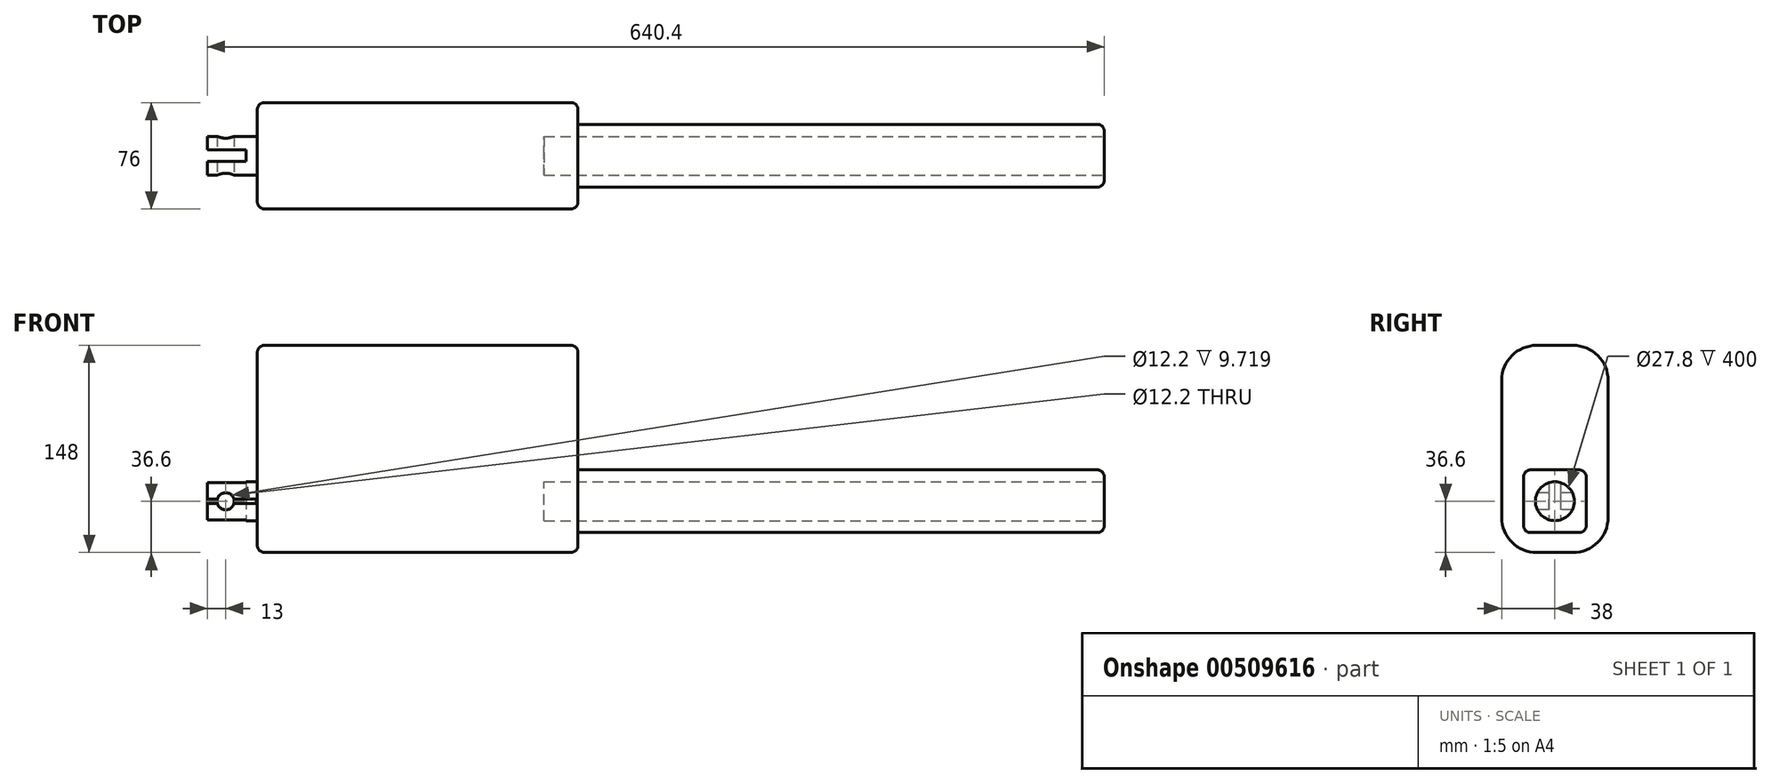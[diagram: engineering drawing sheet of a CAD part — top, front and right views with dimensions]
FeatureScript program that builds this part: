
annotation { "Feature Type Name" : "Feature", "Feature Type Description" : "" }
export const myFeature = defineFeature(function(context is Context, id is Id, definition is map)
    precondition{}
    {
        {
            var Q0;
            Q0=qCreatedBy(makeId("Front.planeOp"),FACE);
            var sketch = newSketch(context, id + "F0", { "sketchPlane" : qUnion([Q0])});
            skLineSegment(sketch, "E0.bottom", {"start": v(-114.5, 74) * mm, "end": v(114.5, 74) * mm});
            skLineSegment(sketch, "E0.top", {"start": v(-114.5, -74) * mm, "end": v(114.5, -74) * mm});
            skLineSegment(sketch, "E0.left", {"start": v(-114.5, 74) * mm, "end": v(-114.5, -74) * mm});
            skLineSegment(sketch, "E0.right", {"start": v(114.5, 74) * mm, "end": v(114.5, -74) * mm});
            skPoint(sketch, "E0.middle", {"position": v(0, 0) * mm});
            skSolve(sketch);
        }
        {
            var Q0;
            Q0=makeQuery(id+"F0.imprint","IMPRINT",FACE,{"disambiguationData":[TD([[makeQuery(id+"F0.imprint","IMPRINT",EDGE,{"derivedFrom":sQuery(id+"F0.wireOp",EDGE,"E0.bottom")}),-1.0]])]});
            extrude(context, id + "F1", {"entities" : qUnion([Q0]), "endBound" : BoundingType.SYMMETRIC, "depth" : 76 * mm});
        }
        {
            var Q0;
            Q0=makeQuery(id+"F1.opExtrude","SWEPT_FACE",FACE,{"disambiguationData":[OSD([sQuery(id+"F0.wireOp",EDGE,"E0.left")])]});
            var sketch = newSketch(context, id + "F2", { "sketchPlane" : qUnion([Q0])});
            skLineSegment(sketch, "E1", {"start": v(0, -74) * mm, "end": v(0, -37.4) * mm});
            skPoint(sketch, "E1.endSnap0", {"position": v(0, -74) * mm});
            skCircle(sketch, "E2", {"center": v(0, -37.4) * mm, "radius": 13.9 * mm});
            skSolve(sketch);
        }
        {
            var Q0;
            Q0=makeQuery(id+"F2.imprint","IMPRINT",FACE,{"disambiguationData":[TD([[makeQuery(id+"F2.imprint","IMPRINT",EDGE,{"derivedFrom":sQuery(id+"F2.wireOp",EDGE,"E2")}),1.0]])]});
            extrude(context, id + "F3", {"entities" : qUnion([Q0]), "operationType" : NewBodyOperationType.ADD, "depth" : 35.6 * mm});
        }
        {
            var Q0;
            Q0=makeQuery(id+"F3.opExtrude","CAP_FACE",FACE,{"disambiguationData":[OSD([sQuery(id+"F2.wireOp",EDGE,"E2")])],"isStart":false});
            var sketch = newSketch(context, id + "F4", { "sketchPlane" : qUnion([Q0])});
            skLineSegment(sketch, "E3.left", {"start": v(-13.82, -35.9) * mm, "end": v(-13.82, -38.9) * mm});
            skLineSegment(sketch, "E3.right", {"start": v(13.82, -35.9) * mm, "end": v(13.82, -38.9) * mm});
            skPoint(sketch, "E3.middle", {"position": v(0, -37.4) * mm});
            skSolve(sketch);
        }
        {
            var Q0;
            {var subQ0=sQuery(id+"F4.wireOp",EDGE,"E3.right");Q0=makeQuery(id+"F4.imprint","IMPRINT",FACE,{"disambiguationData":[TD([[makeQuery(id+"F4.imprint","IMPRINT",EDGE,{"derivedFrom":subQ0}),1.0]])]});}
            extrude(context, id + "F5", {"entities" : qUnion([Q0]), "operationType" : NewBodyOperationType.REMOVE, "oppositeDirection" : true, "depth" : 35 * mm});
        }
        {
            var Q0;
            Q0=makeQuery(id+"F5.boolean.opBoolean","COPY",FACE,{"derivedFrom":makeQuery(id+"F5.opExtrude","SWEPT_FACE",FACE,{"disambiguationData":[OSD([sQuery(id+"F4.wireOp",EDGE,"E3.right")])]})});
            var sketch = newSketch(context, id + "F6", { "sketchPlane" : qUnion([Q0])});
            skLineSegment(sketch, "E4", {"start": v(-150.1, -37.4) * mm, "end": v(-137.1, -37.4) * mm});
            skSolve(sketch);
        }
        {
            var Q0;
            Q0=sQuery(id+"F6.wireOp",VERTEX,"E4.end");
            var Q1;
            Q1=makeQuery(id+"F1.opExtrude","SWEPT_BODY",BODY,{"disambiguationData":[OSD([sQuery(id+"F0.wireOp",EDGE,"E0.bottom"),sQuery(id+"F0.wireOp",EDGE,"E0.top"),sQuery(id+"F0.wireOp",EDGE,"E0.left"),sQuery(id+"F0.wireOp",EDGE,"E0.right")])]});
            hole(context, id + "F7", {"style" : HoleStyle.SIMPLE, "endStyle" : HoleEndStyle.THROUGH, "holeDiameter" : 12.2 * mm, "isTappedThrough" : true, "tappedDepth" : 12 * mm, "tapClearance" : 3, "locations" : qUnion([Q0]), "scope" : qUnion([Q1])});
        }
        {
            var Q0;
            Q0=makeQuery(id+"F1.opExtrude","SWEPT_FACE",FACE,{"disambiguationData":[OSD([sQuery(id+"F0.wireOp",EDGE,"E0.right")])]});
            var sketch = newSketch(context, id + "F8", { "sketchPlane" : qUnion([Q0])});
            skLineSegment(sketch, "E5", {"start": v(0, -74) * mm, "end": v(0, -37.4) * mm});
            skLineSegment(sketch, "E6.bottom", {"start": v(-22.4, -15) * mm, "end": v(22.4, -15) * mm});
            skLineSegment(sketch, "E6.top", {"start": v(-22.4, -59.8) * mm, "end": v(22.4, -59.8) * mm});
            skLineSegment(sketch, "E6.left", {"start": v(-22.4, -15) * mm, "end": v(-22.4, -59.8) * mm});
            skLineSegment(sketch, "E6.right", {"start": v(22.4, -15) * mm, "end": v(22.4, -59.8) * mm});
            skPoint(sketch, "E6.middle", {"position": v(0, -37.4) * mm});
            skSolve(sketch);
        }
        {
            var Q0;
            Q0=makeQuery(id+"F8.imprint","IMPRINT",FACE,{"disambiguationData":[TD([[makeQuery(id+"F8.imprint","IMPRINT",EDGE,{"derivedFrom":sQuery(id+"F8.wireOp",EDGE,"E6.bottom")}),-1.0]])]});
            extrude(context, id + "F9", {"entities" : qUnion([Q0]), "operationType" : NewBodyOperationType.ADD, "depth" : 375.8 * mm});
        }
        {
            var Q0;
            Q0=makeQuery(id+"F9.opExtrude","CAP_FACE",FACE,{"disambiguationData":[OSD([sQuery(id+"F8.wireOp",EDGE,"E6.bottom"),sQuery(id+"F8.wireOp",EDGE,"E6.top"),sQuery(id+"F8.wireOp",EDGE,"E6.left"),sQuery(id+"F8.wireOp",EDGE,"E6.right")])],"isStart":false});
            var sketch = newSketch(context, id + "F10", { "sketchPlane" : qUnion([Q0])});
            skLineSegment(sketch, "E7", {"start": v(0, -15) * mm, "end": v(0, -37.4) * mm});
            skPoint(sketch, "E7.endSnap0", {"position": v(0, -15) * mm});
            skCircle(sketch, "E8", {"center": v(0, -37.4) * mm, "radius": 13.9 * mm});
            skSolve(sketch);
        }
        {
            var Q0;
            Q0=makeQuery(id+"F1.opExtrude","CAP_EDGE",EDGE,{"disambiguationData":[OSD([sQuery(id+"F0.wireOp",EDGE,"E0.bottom")])],"isStart":false});
            var Q1;
            Q1=makeQuery(id+"F1.opExtrude","CAP_EDGE",EDGE,{"disambiguationData":[OSD([sQuery(id+"F0.wireOp",EDGE,"E0.bottom")])],"isStart":true});
            var Q2;
            Q2=makeQuery(id+"F1.opExtrude","CAP_EDGE",EDGE,{"disambiguationData":[OSD([sQuery(id+"F0.wireOp",EDGE,"E0.top")])],"isStart":false});
            var Q3;
            Q3=makeQuery(id+"F1.opExtrude","CAP_EDGE",EDGE,{"disambiguationData":[OSD([sQuery(id+"F0.wireOp",EDGE,"E0.top")])],"isStart":true});
            fillet(context, id + "F11", {"entities" : qUnion([Q0, Q1, Q2, Q3]), "radius" : 25 * mm, "tangentPropagation" : true, "allowEdgeOverflow" : false});
        }
        {
            var Q0;
            Q0=makeQuery(id+"F9.opExtrude","SWEPT_EDGE",EDGE,{"disambiguationData":[OSD([sQuery(id+"F8.wireOp",EDGE,"E6.bottom"),sQuery(id+"F8.wireOp",EDGE,"E6.left")])]});
            var Q1;
            Q1=makeQuery(id+"F9.opExtrude","SWEPT_EDGE",EDGE,{"disambiguationData":[OSD([sQuery(id+"F8.wireOp",EDGE,"E6.bottom"),sQuery(id+"F8.wireOp",EDGE,"E6.right")])]});
            var Q2;
            Q2=makeQuery(id+"F9.opExtrude","SWEPT_EDGE",EDGE,{"disambiguationData":[OSD([sQuery(id+"F8.wireOp",EDGE,"E6.top"),sQuery(id+"F8.wireOp",EDGE,"E6.left")])]});
            var Q3;
            Q3=makeQuery(id+"F9.opExtrude","SWEPT_EDGE",EDGE,{"disambiguationData":[OSD([sQuery(id+"F8.wireOp",EDGE,"E6.top"),sQuery(id+"F8.wireOp",EDGE,"E6.right")])]});
            var Q4;
            Q4=makeQuery(id+"F1.opExtrude","CAP_EDGE",EDGE,{"disambiguationData":[OSD([sQuery(id+"F0.wireOp",EDGE,"E0.right")])],"isStart":true});
            var Q5;
            Q5=makeQuery(id+"F1.opExtrude","CAP_EDGE",EDGE,{"disambiguationData":[OSD([sQuery(id+"F0.wireOp",EDGE,"E0.left")])],"isStart":true});
            var Q6;
            Q6=makeQuery(id+"F9.opExtrude","CAP_EDGE",EDGE,{"disambiguationData":[OSD([sQuery(id+"F8.wireOp",EDGE,"E6.right")])],"isStart":false});
            var Q7;
            Q7=makeQuery(id+"F9.opExtrude","CAP_FACE",FACE,{"disambiguationData":[OSD([sQuery(id+"F8.wireOp",EDGE,"E6.bottom"),sQuery(id+"F8.wireOp",EDGE,"E6.top"),sQuery(id+"F8.wireOp",EDGE,"E6.left"),sQuery(id+"F8.wireOp",EDGE,"E6.right")])],"isStart":false});
            fillet(context, id + "F12", {"entities" : qUnion([Q0, Q1, Q2, Q3, Q4, Q5, Q6, Q7]), "radius" : 5 * mm, "tangentPropagation" : true, "allowEdgeOverflow" : false});
        }
        {
            var Q0;
            Q0=makeQuery(id+"F10.imprint","IMPRINT",FACE,{"disambiguationData":[TD([[makeQuery(id+"F10.imprint","IMPRINT",EDGE,{"derivedFrom":sQuery(id+"F10.wireOp",EDGE,"E8")}),1.0]])]});
            extrude(context, id + "F13", {"entities" : qUnion([Q0]), "operationType" : NewBodyOperationType.REMOVE, "oppositeDirection" : true, "depth" : 400 * mm});
        }
        {
            var Q0;
            Q0=makeQuery(id+"F3.opExtrude","CAP_FACE",FACE,{"disambiguationData":[OSD([sQuery(id+"F2.wireOp",EDGE,"E2")])],"isStart":false});
            var sketch = newSketch(context, id + "F14", { "sketchPlane" : qUnion([Q0])});
            skLineSegment(sketch, "E9.bottom", {"start": v(-4.1, 11.75) * mm, "end": v(4.1, 11.75) * mm});
            skLineSegment(sketch, "E9.top", {"start": v(-4.1, -86.55) * mm, "end": v(4.1, -86.55) * mm});
            skLineSegment(sketch, "E9.left", {"start": v(-4.1, 11.75) * mm, "end": v(-4.1, -86.55) * mm});
            skLineSegment(sketch, "E9.right", {"start": v(4.1, 11.75) * mm, "end": v(4.1, -86.55) * mm});
            skPoint(sketch, "E9.middle", {"position": v(0, -37.4) * mm});
            skSolve(sketch);
        }
        {
            var Q0;
            {var subQ0=sQuery(id+"F14.wireOp",EDGE,"E9.left");var subQ1=makeQuery(id+"F3.opExtrude","CAP_EDGE",EDGE,{"disambiguationData":[OSD([sQuery(id+"F2.wireOp",EDGE,"E2")])],"isStart":false});var subQ2=makeQuery(id+"F14.imprint","INTERSECT",VERTEX,{"disambiguationData":[OD(0.0)],"derivedFrom":[subQ1,subQ0]});Q0=makeQuery(id+"F14.imprint","IMPRINT",FACE,{"disambiguationData":[TD([[makeQuery(id+"F14.imprint","IMPRINT",EDGE,{"disambiguationData":[TD([[subQ2,-1.0]])],"derivedFrom":subQ0}),1.0]])]});}
            extrude(context, id + "F15", {"entities" : qUnion([Q0]), "operationType" : NewBodyOperationType.REMOVE, "oppositeDirection" : true, "depth" : 27.5 * mm});
        }
    });
